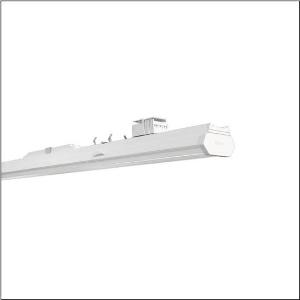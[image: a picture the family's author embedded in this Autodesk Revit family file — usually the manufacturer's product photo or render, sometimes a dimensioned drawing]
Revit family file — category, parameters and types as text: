
# Revit family: licross_r__21_protected_mo_52td1bvn455g_6e17
name_source: partatom
category: Lighting Fixtures
units: mm (PartAtom-declared; Revit-internal decimal feet)

## family parameters
Cut with Voids When Loaded = No
Host = Face
Light Source = No
Part Type = Normal
Room Calculation Point = No
Round Connector Dimension = Use Diameter
Shared = No

## types (1)
- --- (1 x LED, 5500 lm, 32.3 W, 4000K)
    Apparent Load = 32 VA
    CIE Flux Codes = 54 82 95 97 100
    Color Rendering = 80
    Color Temperature = 4000K
    Default Elevation = 1800 mm
    Description = Licross® 21 Protected MO, luminaire insert, of sheet steel, galvanised, coil coated, white, length: 1.500mm, width: 90mm, height: 101mm, LED rated luminous flux: 5.500lm, light colour: 840, control gear: DALI 2, CLO, with plug, 5-pole, with phase selection, mains connection: 220..240V, AC, 50/60Hz, start of lifetime: 32W, end of service life: 38W, halogen-free wiring, primary optical cover: cover, of PMMA, light emission: direct distribution, primary light characteristic: symmetric, protection rating (complete): IP54, insulation class (complete): insulation class I (protective earthing), certification: CE, ENEC, VDE, UKCA, protection symbol: D if used in an environment with non-conductive dust loads with corresponding accessories, impact resistance: IK06, permissible ambient temperature for indoor applications: -25..+45°C, corresponds to IFS (International Featured Standards) requirements for safety and quality in the food industry, reducing of maximum allowable ambient temperature of 5°C with ceiling mounting, LABS conformity tested according to VDMA 24364:2018-05, packaging unit: 1 piece
    Height = 92 mm
    Lamp = 1 x LED
    Lamp Light Flux = 5500 lm
    Lamp Power = 32.3 W
    Lamp count = 1
    Length = 1500 mm
    Luminous efficacy = 170 lm/W
    Manufacturer = Siteco
    ModVariant = No
    Model = 52TD1BVN455G
    Mounting Place = Ceiling
    Mounting Type = Pendant
    Number of Poles = 1
    OnlyDefault = Yes
    Power Factor = 1
    Product Name = Licross® 21 Protected MO
    Product group = luminaire insert
    ProductGroupID = 901
    Protection Class = Protection class I
    Protection Degree = IP 54
    RLX_Detail_Level = 1
    RLX_Emergency_Light_Flux = 0 lm
    RLX_Emergency_Type = 0
    RLX_Emergency_Type_DB = No
    RlxData = <blob elided: 23917 chars, md5=984530a4>
    Socket = socket
    Standby Power = 0 W
    System Light Flux = 5500 lm
    System Power = 32 W
    Type Comments = factory setting: luminous flux: 100 % | dim-lin: 254 | 219 mA
    Type Image = l_1256148.jpg
    URL = http://relux.com
    VarID = @adj_035135
    Voltage = 0 V
    Weight = 0.00 kg
    Width = 88 mm

## geometry (parser evidence)
native form markers: Blend x4, Sweep x11
no freeform markers — native parametric forms only
